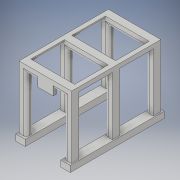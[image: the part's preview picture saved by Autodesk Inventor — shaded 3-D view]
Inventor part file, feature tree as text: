
AUTODESK INVENTOR PART (.ipt)
format: ipt  version: 2018 (Build 220112000, 112)  size: 270,848 bytes
history: native  units: in
note: dims shown in document units (in); Inventor stores cm internally (conversion verified against a paired STEP export)
features: extrude x7, sketch x7, fillet x2, other x1
ambient origin geometry x8: Origin, YZ Plane, XZ Plane, XY Plane, X Axis, Y Axis, Z Axis, Center Point
bodies: Body1 (feature_tree)
feature tree (17):
  other  "Sólido1"
  extrude  "Extrusión1"  Depth=1.0in
  extrude  "Extrusión2"  Depth=1.1851in
  extrude  "Extrusión3"  Depth=1.185in
  extrude  "Extrusión4"  Depth=1.185in
  extrude  "Extrusión5"  Depth=1.1851in
  fillet  "Empalme1"  Radius=1.1851in
  extrude  "Extrusión6"  Depth=1.185in
  extrude  "Extrusión7"  Depth=1.185in
  fillet  "Empalme2"  Radius=6.0in
  sketch  "Boceto1"  dims[d0=1.5in d1=1.0in]
  sketch  "Boceto2"  dims[d2=15.0in d3=0.0in d4=1.1851in]
  sketch  "Boceto3"  dims[d5=1.185in d6=14.0445in]
  sketch  "Boceto4"  dims[d7=0.75in d8=1.185in]
  sketch  "Boceto5"  dims[d9=1.185in d10=0.955in d11=1.1851in]
  sketch  "Boceto6"  dims[d12=10.0in d13=0.0in d14=1.185in]
  sketch  "Boceto7"  dims[d15=1.185in d16=1.185in d17=6.0in d18=0.0in d19=1.185in d20=1.185in d21=1.185in d22=1.185in d23=1.185in d24=1.185in d25=10.0in d26=0.0in d27=1.5in d28=1.0in d29=7.2in d30=0.9464in d31=2.4932in d32=5.4697in d33=0.5in d34=0.0in d35=0.5in d36=0.5in d37=0.0in d38=0.5in d39=0.0in d40=0.5in]
